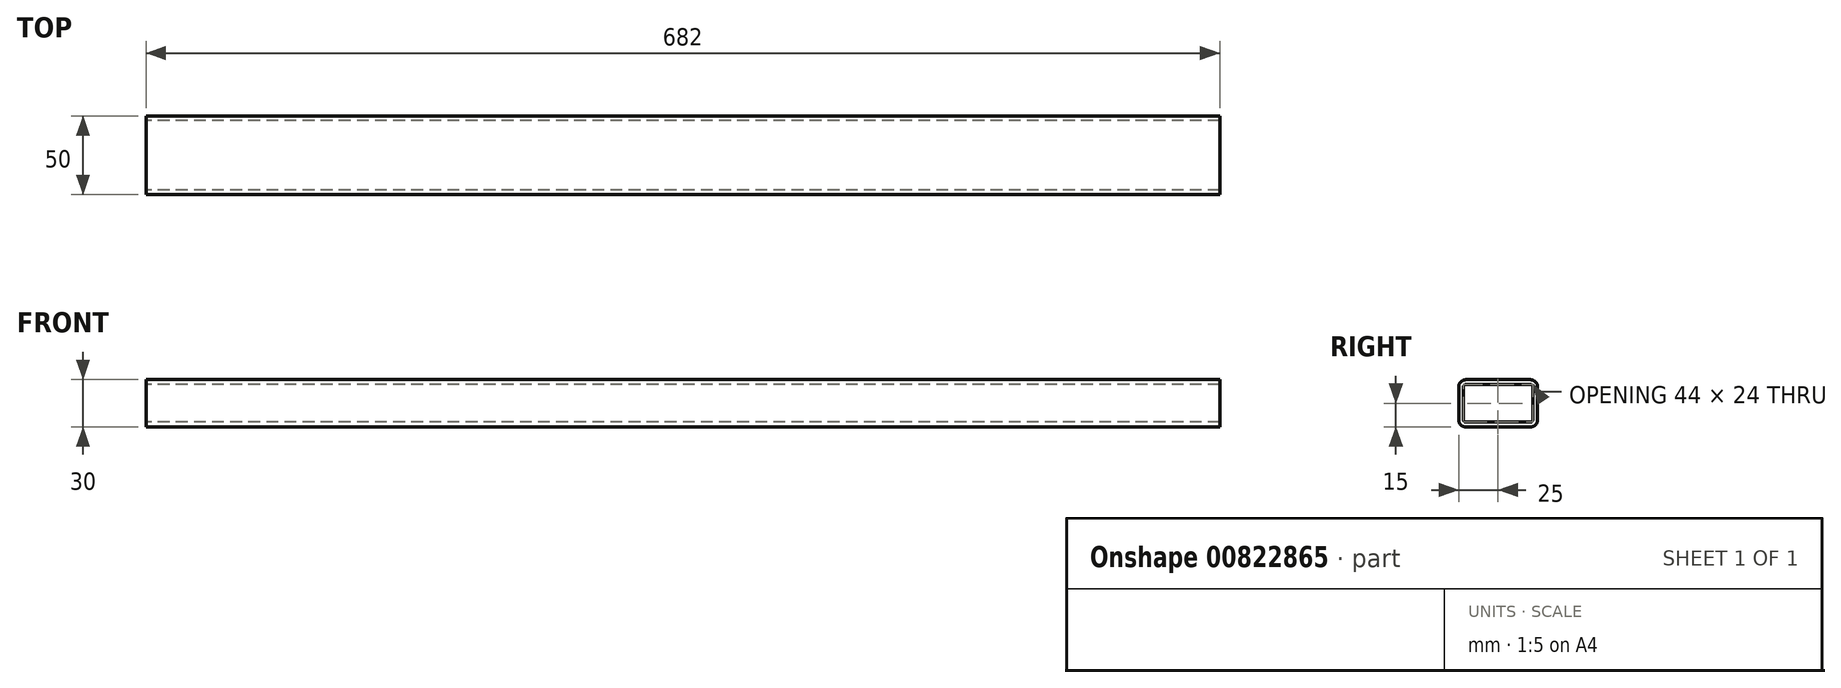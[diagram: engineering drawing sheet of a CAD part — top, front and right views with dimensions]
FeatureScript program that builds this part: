
annotation { "Feature Type Name" : "Feature", "Feature Type Description" : "" }
export const myFeature = defineFeature(function(context is Context, id is Id, definition is map)
    precondition{}
    {
        {
            var Q0;
            Q0=qCreatedBy(makeId("Right.planeOp"),FACE);
            var sketch = newSketch(context, id + "F0", { "sketchPlane" : qUnion([Q0])});
            skLineSegment(sketch, "E0.bottom", {"start": v(-25, -15) * mm, "end": v(25, -15) * mm});
            skLineSegment(sketch, "E0.top", {"start": v(-25, 15) * mm, "end": v(25, 15) * mm});
            skLineSegment(sketch, "E0.left", {"start": v(-25, -15) * mm, "end": v(-25, 15) * mm});
            skLineSegment(sketch, "E0.right", {"start": v(25, -15) * mm, "end": v(25, 15) * mm});
            skPoint(sketch, "E0.middle", {"position": v(0, 0) * mm});
            skLineSegment(sketch, "E1.0", {"start": v(-22, 12) * mm, "end": v(22, 12) * mm});
            skLineSegment(sketch, "E1.1", {"start": v(-22, -12) * mm, "end": v(-22, 12) * mm});
            skLineSegment(sketch, "E1.2", {"start": v(-22, -12) * mm, "end": v(22, -12) * mm});
            skLineSegment(sketch, "E1.3", {"start": v(22, -12) * mm, "end": v(22, 12) * mm});
            skSolve(sketch);
        }
        {
            var Q0;
            Q0=qSketchRegion(id+"F0",true);
            extrude(context, id + "F1", {"entities" : qUnion([Q0]), "endBound" : BoundingType.SYMMETRIC, "depth" : 682 * mm, "offsetDistance" : 25 * mm});
        }
        {
            var Q0;
            Q0=makeQuery(id+"F1.opExtrude","SWEPT_EDGE",EDGE,{"disambiguationData":[OSD([sQuery(id+"F0.wireOp",EDGE,"E1.1"),sQuery(id+"F0.wireOp",EDGE,"E1.2")])]});
            var Q1;
            Q1=makeQuery(id+"F1.opExtrude","SWEPT_EDGE",EDGE,{"disambiguationData":[OSD([sQuery(id+"F0.wireOp",EDGE,"E1.0"),sQuery(id+"F0.wireOp",EDGE,"E1.1")])]});
            var Q2;
            Q2=makeQuery(id+"F1.opExtrude","SWEPT_EDGE",EDGE,{"disambiguationData":[OSD([sQuery(id+"F0.wireOp",EDGE,"E1.2"),sQuery(id+"F0.wireOp",EDGE,"E1.3")])]});
            var Q3;
            Q3=makeQuery(id+"F1.opExtrude","SWEPT_EDGE",EDGE,{"disambiguationData":[OSD([sQuery(id+"F0.wireOp",EDGE,"E1.0"),sQuery(id+"F0.wireOp",EDGE,"E1.3")])]});
            fillet(context, id + "F2", {"entities" : qUnion([Q0, Q1, Q2, Q3]), "radius" : 1.5 * mm, "tangentPropagation" : true, "allowEdgeOverflow" : false});
        }
        {
            var Q0;
            Q0=makeQuery(id+"F1.opExtrude","SWEPT_EDGE",EDGE,{"disambiguationData":[OSD([sQuery(id+"F0.wireOp",EDGE,"E0.top"),sQuery(id+"F0.wireOp",EDGE,"E0.left")])]});
            var Q1;
            Q1=makeQuery(id+"F1.opExtrude","SWEPT_EDGE",EDGE,{"disambiguationData":[OSD([sQuery(id+"F0.wireOp",EDGE,"E0.bottom"),sQuery(id+"F0.wireOp",EDGE,"E0.left")])]});
            var Q2;
            Q2=makeQuery(id+"F1.opExtrude","SWEPT_EDGE",EDGE,{"disambiguationData":[OSD([sQuery(id+"F0.wireOp",EDGE,"E0.bottom"),sQuery(id+"F0.wireOp",EDGE,"E0.right")])]});
            var Q3;
            Q3=makeQuery(id+"F1.opExtrude","SWEPT_EDGE",EDGE,{"disambiguationData":[OSD([sQuery(id+"F0.wireOp",EDGE,"E0.top"),sQuery(id+"F0.wireOp",EDGE,"E0.right")])]});
            fillet(context, id + "F3", {"entities" : qUnion([Q0, Q1, Q2, Q3]), "radius" : 4.5 * mm, "tangentPropagation" : true, "allowEdgeOverflow" : false});
        }
    });
